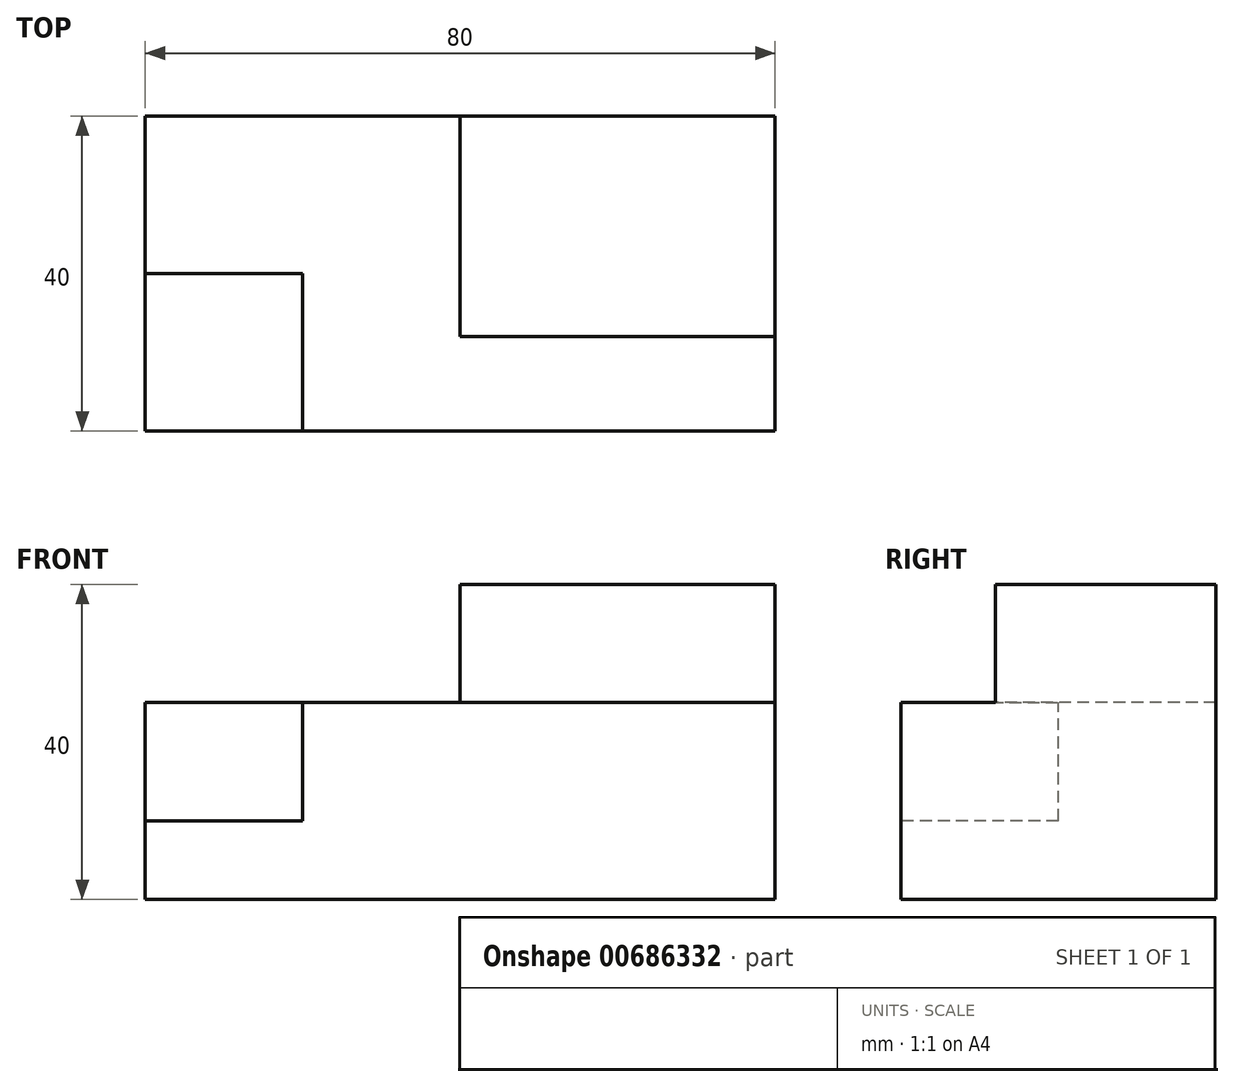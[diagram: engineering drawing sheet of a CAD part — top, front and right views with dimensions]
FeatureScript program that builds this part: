
annotation { "Feature Type Name" : "Feature", "Feature Type Description" : "" }
export const myFeature = defineFeature(function(context is Context, id is Id, definition is map)
    precondition{}
    {
        {
            var Q0;
            Q0=qCreatedBy(makeId("Top.planeOp"),FACE);
            var sketch = newSketch(context, id + "F0", { "sketchPlane" : qUnion([Q0])});
            skLineSegment(sketch, "E0.bottom", {"start": v(-41.23, 20.6) * mm, "end": v(38.77, 20.6) * mm});
            skLineSegment(sketch, "E0.top", {"start": v(-41.23, -19.4) * mm, "end": v(38.77, -19.4) * mm});
            skLineSegment(sketch, "E0.left", {"start": v(-41.23, 20.6) * mm, "end": v(-41.23, -19.4) * mm});
            skLineSegment(sketch, "E0.right", {"start": v(38.77, 20.6) * mm, "end": v(38.77, -19.4) * mm});
            skLineSegment(sketch, "E1.bottom", {"start": v(-41.23, -19.4) * mm, "end": v(-21.23, -19.4) * mm});
            skLineSegment(sketch, "E1.top", {"start": v(-41.23, 0.6) * mm, "end": v(-21.23, 0.6) * mm});
            skLineSegment(sketch, "E1.left", {"start": v(-41.23, -19.4) * mm, "end": v(-41.23, 0.6) * mm});
            skLineSegment(sketch, "E1.right", {"start": v(-21.23, -19.4) * mm, "end": v(-21.23, 0.6) * mm});
            skLineSegment(sketch, "E2.bottom", {"start": v(-1.23, 20.6) * mm, "end": v(38.77, 20.6) * mm});
            skLineSegment(sketch, "E2.top", {"start": v(-1.23, -7.4) * mm, "end": v(38.77, -7.4) * mm});
            skLineSegment(sketch, "E2.left", {"start": v(-1.23, 20.6) * mm, "end": v(-1.23, -7.4) * mm});
            skLineSegment(sketch, "E2.right", {"start": v(38.77, 20.6) * mm, "end": v(38.77, -7.4) * mm});
            skSolve(sketch);
        }
        {
            var Q0;
            Q0 = qSketchRegion(id + "F0", true);
            extrude(context, id + "F1", {"entities" : qUnion([Q0]), "depth" : 25 * mm, "offsetDistance" : 25.4 * mm});
        }
        {
            var Q0;
            Q0=makeQuery(id+"F1.opExtrude","CAP_FACE",FACE,{"disambiguationData":[OSD([sQuery(id+"F0.wireOp",EDGE,"E0.bottom"),sQuery(id+"F0.wireOp",EDGE,"E0.top"),sQuery(id+"F0.wireOp",EDGE,"E0.left"),sQuery(id+"F0.wireOp",EDGE,"E0.right"),sQuery(id+"F0.wireOp",EDGE,"E1.bottom"),sQuery(id+"F0.wireOp",EDGE,"E1.left"),sQuery(id+"F0.wireOp",EDGE,"E2.bottom"),sQuery(id+"F0.wireOp",EDGE,"E2.right")])],"isStart":false});
            var sketch = newSketch(context, id + "F2", { "sketchPlane" : qUnion([Q0])});
            skLineSegment(sketch, "E3.bottom", {"start": v(-41.23, -19.4) * mm, "end": v(-21.23, -19.4) * mm});
            skLineSegment(sketch, "E3.top", {"start": v(-41.23, 0.6) * mm, "end": v(-21.23, 0.6) * mm});
            skLineSegment(sketch, "E3.left", {"start": v(-41.23, -19.4) * mm, "end": v(-41.23, 0.6) * mm});
            skLineSegment(sketch, "E3.right", {"start": v(-21.23, -19.4) * mm, "end": v(-21.23, 0.6) * mm});
            skSolve(sketch);
        }
        {
            var Q0;
            Q0 = qSketchRegion(id + "F2", true);
            extrude(context, id + "F3", {"entities" : qUnion([Q0]), "operationType" : NewBodyOperationType.REMOVE, "oppositeDirection" : true, "depth" : 15 * mm, "offsetDistance" : 25.4 * mm});
        }
        {
            var Q0;
            Q0=makeQuery(id+"F1.opExtrude","CAP_FACE",FACE,{"disambiguationData":[OSD([sQuery(id+"F0.wireOp",EDGE,"E0.bottom"),sQuery(id+"F0.wireOp",EDGE,"E0.top"),sQuery(id+"F0.wireOp",EDGE,"E0.left"),sQuery(id+"F0.wireOp",EDGE,"E0.right"),sQuery(id+"F0.wireOp",EDGE,"E1.bottom"),sQuery(id+"F0.wireOp",EDGE,"E1.left"),sQuery(id+"F0.wireOp",EDGE,"E2.bottom"),sQuery(id+"F0.wireOp",EDGE,"E2.right")])],"isStart":false});
            var sketch = newSketch(context, id + "F4", { "sketchPlane" : qUnion([Q0])});
            skLineSegment(sketch, "E4.bottom", {"start": v(-1.23, 20.6) * mm, "end": v(38.77, 20.6) * mm});
            skLineSegment(sketch, "E4.top", {"start": v(-1.23, -7.4) * mm, "end": v(38.77, -7.4) * mm});
            skLineSegment(sketch, "E4.left", {"start": v(-1.23, 20.6) * mm, "end": v(-1.23, -7.4) * mm});
            skLineSegment(sketch, "E4.right", {"start": v(38.77, 20.6) * mm, "end": v(38.77, -7.4) * mm});
            skSolve(sketch);
        }
        {
            var Q0;
            Q0 = qSketchRegion(id + "F4", true);
            var Q1;
            Q1=makeQuery(id+"F4.imprint","IMPRINT",FACE,{"disambiguationData":[TD([[makeQuery(id+"F4.imprint","IMPRINT",EDGE,{"derivedFrom":sQuery(id+"F4.wireOp",EDGE,"E4.bottom")}),-1.0]])]});
            extrude(context, id + "F5", {"entities" : qUnion([Q0, Q1]), "operationType" : NewBodyOperationType.ADD, "depth" : 15 * mm, "offsetDistance" : 25.4 * mm});
        }
    });
